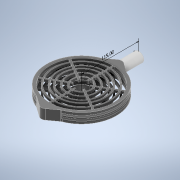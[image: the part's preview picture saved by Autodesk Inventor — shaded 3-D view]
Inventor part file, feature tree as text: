
AUTODESK INVENTOR PART (.ipt)
format: ipt  version: 2021 (Build 250183000, 183)  size: 599,040 bytes
history: native  units: mm
features: extrude x9, sketch x9, other x3, fillet x2, plane x2
ambient origin geometry x8: Origin, YZ Plane, XZ Plane, XY Plane, X Axis, Y Axis, Z Axis, Center Point
bodies: Solid1 (feature_tree)
feature tree (25):
  other  "Annotations"
  extrude  "Extrusion1"  Depth=140.0mm
  extrude  "Extrusion2"  Depth=55.0mm
  fillet  "Fillet1"  Radius=60.0mm
  fillet  "Fillet2"  Radius=75.0mm
  extrude  "Extrusion3"  Depth=90.0mm
  extrude  "Extrusion4"  Depth=110.0mm
  extrude  "Extrusion5"  Depth=5.0mm
  plane  "Work Plane1"
  extrude  "Extrusion6"  Depth=10.0mm
  extrude  "Extrusion7"  Depth=30.0mm TaperAngle=360.0deg
  extrude  "Extrusion8"  Depth=50.0mm
  plane  "Work Plane2"
  extrude  "Extrusion9"  Depth=10.0mm TaperAngle=360.0deg
  sketch  "Sketch1"  dims[d0=128.0mm d1=140.0mm]
  sketch  "Sketch2"  dims[d2=40.0mm d3=55.0mm d4=60.0mm d5=75.0mm]
  sketch  "Sketch3"  dims[d6=80.0mm d7=90.0mm]
  sketch  "Sketch4"  dims[d8=95.0mm d9=110.0mm]
  sketch  "Sketch5"  dims[d10=115.0mm d11=5.0mm]
  sketch  "Sketch7"  dims[d12=10.0mm d13=67.0mm]
  sketch  "Sketch8"  dims[d14=0.0mm d15=30.0mm d17=360.0deg]
  sketch  "Sketch9"  dims[d19=5.0mm d20=0.0mm d21=50.0mm]
  sketch  "Sketch10"  dims[d23=18.0mm d24=20.0mm d26=360.0deg d28=15.0mm d29=0.0mm d30=10.0mm d31=10.0mm d32=5.0mm d33=2.0mm d34=0.0mm d35=25.0mm d36=30.0mm d37=0.0mm d38=18.0mm d39=10.0mm d40=0.0mm d41=5.0mm d42=0.0mm d43=5.0mm d44=140.0mm d45=128.0mm d46=3.0mm d47=0.0mm d49=60.0mm d50=128.0mm d51=140.0mm d52=40.0mm d53=55.0mm d54=60.0mm d55=75.0mm d56=80.0mm d57=90.0mm d58=95.0mm d59=110.0mm d60=115.0mm d61=1.5mm d62=3.0mm d63=67.0mm d64=0.0mm d65=360.0deg d66=0.0mm d67=5.0mm d68=0.0mm d69=25.0mm d70=5.0mm d71=0.0mm d72=35.0mm d73=-75.0mm d74=20.0mm d75=10.0mm d76=23.957065mm d77=40.0mm d78=0.0mm d79=3.0mm d81=115.0mm d82=0.5mm d83=0.872665mm d84=0.5mm d85=0.872665mm]
  other  "Linear Dimension 1"
  other  "Linear Dimension 2"
